# Revit family: Farola Solar Olintu L galvanizada
name_source: partatom
category: Luminarias
units: mm (PartAtom-declared; Revit-internal decimal feet)

## family parameters
Compartido = Sí
Corte con vacíos al cargar = No
Cota de conector redondo = Diámetro de uso
Origen de luz = No
Punto de cálculo de habitación = No
Se basa en plano de trabajo = No
Siempre vertical = Sí
Tipo de pieza = Normal

## types (1)
- Farola Solar Olintu L galvanizada
    Altura columna extremos = 8000 mm  [stored 26.2467 ft]
    Altura columna planos = 8000 mm  [stored 26.2467 ft]
    Clase eficiencia energética = A++
    Descripción = Farola solar que combina diseño y eficencia
    Descripción de la empresa = Diseñamos, desarrollamos, fabricamos y comercializamos farolas solares que se adaptan a cualquier necesidad.
    Dirección = Parque Tecnológico Miramón - Paseo Mikeletegi 56 - 20009 Donostia/San Sebastián
    Distancia brazo-final de columna = 7000 mm
    Distancia inserto-columa = 7850 mm
    Elevación por defecto = 2000 mm  [stored 6.56168 ft]
    Fabricante = Ekiona
    Gama de acabados = Galvanizado, Fibra de vidrio, Aluminio
    Gama de colores = Blanco, Negro, Gris, Verde bosque, Acero galvanizado
    Garantía = 5 años
    Marcado CE = SÍ
    Modelo = Modelo Olintu
    URL = https://www.ekiona.com
    URL producto = https://ekiona.com

note: [stored X ft] marks values corroborated as IEEE doubles in the binary element streams (Revit-internal decimal feet)

## geometry (parser evidence)
native form markers: Blend x6, Sweep x10
no freeform markers — native parametric forms only
